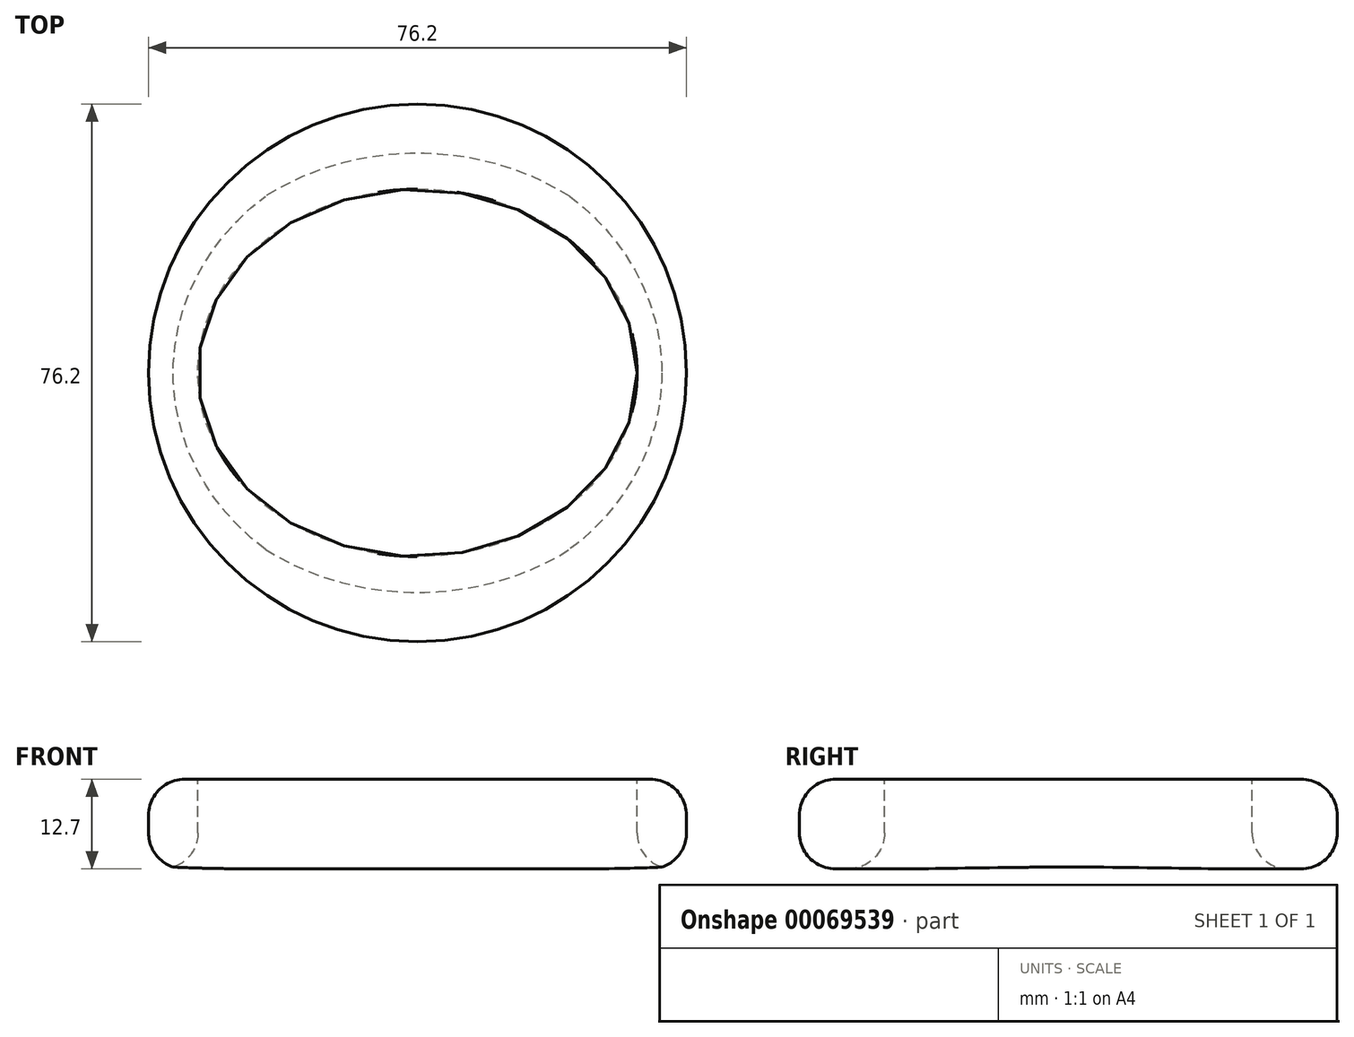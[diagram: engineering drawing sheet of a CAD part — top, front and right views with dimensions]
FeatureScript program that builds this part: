
annotation { "Feature Type Name" : "Feature", "Feature Type Description" : "" }
export const myFeature = defineFeature(function(context is Context, id is Id, definition is map)
    precondition{}
    {
        {
            var Q0;
            Q0=qCreatedBy(makeId("Top.planeOp"),FACE);
            var sketch = newSketch(context, id + "F0", { "sketchPlane" : qUnion([Q0])});
            skEllipse(sketch, "E0", {"center": v(0, 0) * mm, "majorRadius": 38.1 * mm, "minorRadius": 38.1 * mm, "majorAxis": v(1, 0)});
            skSolve(sketch);
        }
        {
            var Q0;
            Q0 = qSketchRegion(id + "F0", true);
            extrude(context, id + "F1", {"entities" : qUnion([Q0]), "depth" : 12.7 * mm});
        }
        {
            var Q0;
            Q0=makeQuery(id+"F1.opExtrude","CAP_FACE",FACE,{"disambiguationData":[OSD([sQuery(id+"F0.wireOp",EDGE,"E0")])],"isStart":false});
            var sketch = newSketch(context, id + "F2", { "sketchPlane" : qUnion([Q0])});
            skEllipse(sketch, "E1", {"center": v(0, 0) * mm, "majorRadius": 31.12 * mm, "minorRadius": 26.04 * mm, "majorAxis": v(1, 0)});
            skSolve(sketch);
        }
        {
            var Q0;
            Q0=makeQuery(id+"F2.imprint","IMPRINT",FACE,{"disambiguationData":[TD([[makeQuery(id+"F2.imprint","IMPRINT",EDGE,{"derivedFrom":sQuery(id+"F2.wireOp",EDGE,"E1")}),1.0]])]});
            extrude(context, id + "F3", {"entities" : qUnion([Q0]), "operationType" : NewBodyOperationType.REMOVE, "endBound" : BoundingType.THROUGH_ALL, "oppositeDirection" : true, "depth" : 25.4 * mm});
        }
        {
            var Q0;
            Q0=makeQuery(id+"F3.boolean.opBoolean","COPY",EDGE,{"derivedFrom":makeQuery(id+"F3.opExtrude","CAP_EDGE",EDGE,{"disambiguationData":[OSD([sQuery(id+"F2.wireOp",EDGE,"E1")])],"isStart":true})});
            var Q1;
            Q1=makeQuery(id+"F1.opExtrude","CAP_EDGE",EDGE,{"disambiguationData":[OSD([sQuery(id+"F0.wireOp",EDGE,"E0")])],"isStart":false});
            var Q2;
            Q2=makeQuery(id+"F1.opExtrude","CAP_EDGE",EDGE,{"disambiguationData":[OSD([sQuery(id+"F0.wireOp",EDGE,"E0")])],"isStart":true});
            var Q3;
            Q3=makeQuery(id+"F3.boolean.opBoolean","INTERSECT",EDGE,{"derivedFrom":[makeQuery(id+"F1.opExtrude","CAP_FACE",FACE,{"disambiguationData":[OSD([sQuery(id+"F0.wireOp",EDGE,"E0")])],"isStart":true}),makeQuery(id+"F3.opExtrude","SWEPT_FACE",FACE,{"disambiguationData":[OSD([sQuery(id+"F2.wireOp",EDGE,"E1")])]})]});
            fillet(context, id + "F4", {"entities" : qUnion([Q0, Q1, Q2, Q3]), "radius" : 5.08 * mm, "tangentPropagation" : true, "allowEdgeOverflow" : false});
        }
    });
